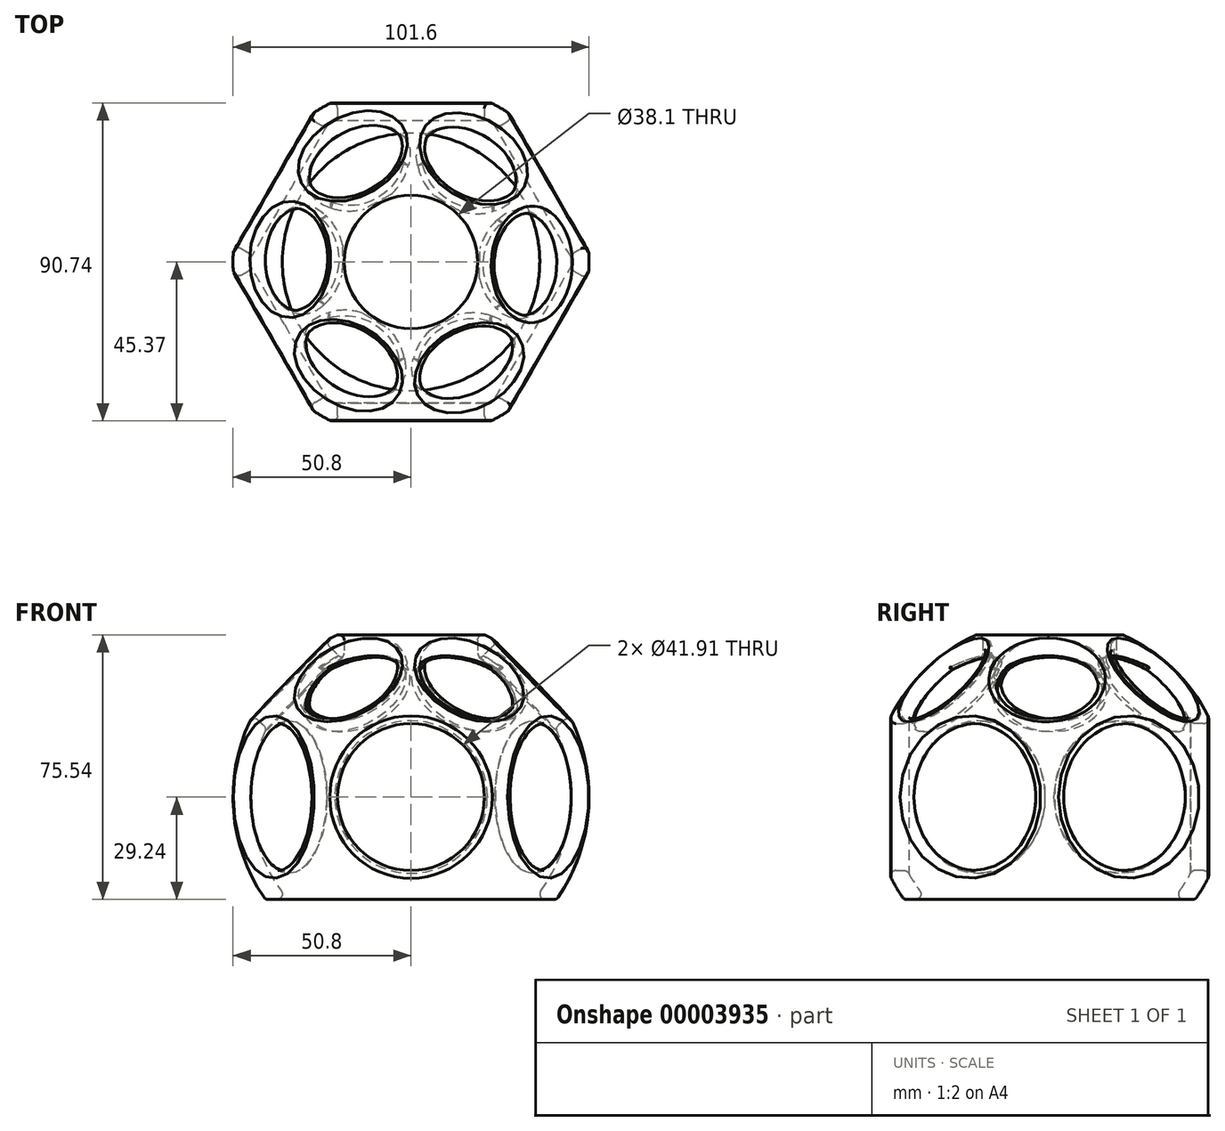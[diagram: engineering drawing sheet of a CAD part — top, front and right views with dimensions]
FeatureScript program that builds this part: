
annotation { "Feature Type Name" : "Feature", "Feature Type Description" : "" }
export const myFeature = defineFeature(function(context is Context, id is Id, definition is map)
    precondition{}
    {
        {
            var Q0;
            Q0=qCreatedBy(makeId("Front.planeOp"),FACE);
            var sketch = newSketch(context, id + "F0", { "sketchPlane" : qUnion([Q0])});
            skArc(sketch, "E0", {"start": v(0, 50.8) * mm, "mid": v(-42.5, 27.81) * mm, "end": v(-46.55, -20.35) * mm});
            skLineSegment(sketch, "E1", {"start": v(-40.94, -20.35) * mm, "end": v(0, 0) * mm, "construction": true});
            skLineSegment(sketch, "E2", {"start": v(0, 0) * mm, "end": v(0, 50.8) * mm, "construction": true});
            skArc(sketch, "E3", {"start": v(-27.63, 36.42) * mm, "mid": v(-44.51, 10.44) * mm, "end": v(-40.94, -20.35) * mm});
            skLineSegment(sketch, "E4", {"start": v(-40.94, -20.35) * mm, "end": v(-46.55, -20.35) * mm});
            skPoint(sketch, "E5.orphan", {"position": v(-45.5, -22.6) * mm});
            skArc(sketch, "E6", {"start": v(-46.55, -20.35) * mm, "mid": v(-44.27, -24.92) * mm, "end": v(-41.54, -29.24) * mm});
            skArc(sketch, "E7", {"start": v(-40.94, -20.35) * mm, "mid": v(-38.3, -24.96) * mm, "end": v(-35.15, -29.24) * mm});
            skLineSegment(sketch, "E8", {"start": v(-41.54, -29.24) * mm, "end": v(-35.15, -29.24) * mm});
            skLineSegment(sketch, "E9", {"start": v(0, 50.8) * mm, "end": v(0, 42.76) * mm});
            skArc(sketch, "E10", {"start": v(0, 42.76) * mm, "mid": v(-14.22, 41.33) * mm, "end": v(-27.63, 36.42) * mm});
            skSolve(sketch);
        }
        {
            var Q0;
            Q0=sQuery(id+"F0.wireOp",EDGE,"E1");
            cPlane(context, id + "F1", {"entities" : qUnion([Q0]), "cplaneType" : CPlaneType.LINE_ANGLE, "offset" : 152.4 * mm, "angle" : 51 * degree, "width" : 152.4 * mm, "height" : 152.4 * mm});
        }
        {
            var Q0;
            Q0=makeQuery(id+"F0.imprint","IMPRINT",FACE,{"disambiguationData":[TD([[makeQuery(id+"F0.imprint","IMPRINT",EDGE,{"derivedFrom":sQuery(id+"F0.wireOp",EDGE,"E0")}),1.0]])]});
            var Q1;
            Q1=makeQuery(id+"F0.imprint","IMPRINT",FACE,{"disambiguationData":[TD([[makeQuery(id+"F0.imprint","IMPRINT",EDGE,{"derivedFrom":sQuery(id+"F0.wireOp",EDGE,"E4")}),1.0]])]});
            var Q2;
            Q2=sQuery(id+"F0.wireOp",EDGE,"E2");
            revolve(context, id + "F2", {"entities" : qUnion([Q0, Q1]), "axis" : qUnion([Q2]), "revolveType" : RevolveType.FULL});
        }
        {
            var Q0;
            Q0=qCreatedBy(makeId("Top.planeOp"),FACE);
            var sketch = newSketch(context, id + "F3", { "sketchPlane" : qUnion([Q0])});
            skCircle(sketch, "E11", {"center": v(0, 0) * mm, "radius": 19.05 * mm});
            skSolve(sketch);
        }
        {
            var Q0;
            Q0=makeQuery(id+"F3.imprint","IMPRINT",FACE,{"disambiguationData":[TD([[makeQuery(id+"F3.imprint","IMPRINT",EDGE,{"derivedFrom":sQuery(id+"F3.wireOp",EDGE,"E11")}),1.0]])]});
            extrude(context, id + "F4", {"entities" : qUnion([Q0]), "operationType" : NewBodyOperationType.REMOVE, "endBound" : BoundingType.SYMMETRIC, "depth" : 101.6 * mm});
        }
        {
            var Q0;
            Q0=qCreatedBy(makeId("Front.planeOp"),FACE);
            var sketch = newSketch(context, id + "F5", { "sketchPlane" : qUnion([Q0])});
            skCircle(sketch, "E12", {"center": v(0, 0) * mm, "radius": 20.96 * mm});
            skSolve(sketch);
        }
        {
            var Q0;
            Q0=makeQuery(id+"F5.imprint","IMPRINT",FACE,{"disambiguationData":[TD([[makeQuery(id+"F5.imprint","IMPRINT",EDGE,{"derivedFrom":sQuery(id+"F5.wireOp",EDGE,"E12")}),1.0]])]});
            var Q1;
            Q1=sQuery(id+"F5.wireOp",EDGE,"E12");
            extrude(context, id + "F6", {"entities" : qUnion([Q0]), "surfaceEntities" : qUnion([Q1]), "depth" : 76.2 * mm});
        }
        {
            var Q0;
            Q0=makeQuery(id+"F6.opExtrude","SWEPT_FACE",FACE,{"disambiguationData":[OSD([sQuery(id+"F5.wireOp",EDGE,"E12")])]});
            var Q1;
            Q1=makeQuery(id+"F6.opExtrude","SWEPT_BODY",BODY,{"disambiguationData":[OSD([sQuery(id+"F5.wireOp",EDGE,"E12")])]});
            var Q2;
            Q2=makeQuery(id+"F4.boolean.opBoolean","COPY",FACE,{"derivedFrom":makeQuery(id+"F4.opExtrude","SWEPT_FACE",FACE,{"disambiguationData":[OSD([sQuery(id+"F3.wireOp",EDGE,"E11")])]})});
            circularPattern(context, id + "F7", {"entities" : qUnion([Q1]), "axis" : qUnion([Q2]), "angle" : 60 * degree, "instanceCount" : 6});
        }
        {
            var Q0;
            Q0=makeQuery(id+"F6.opExtrude","SWEPT_BODY",BODY,{"disambiguationData":[OSD([sQuery(id+"F5.wireOp",EDGE,"E12")])]});
            var Q1;
            Q1=makeQuery(id+"F7.opPattern","COPY",BODY,{"derivedFrom":makeQuery(id+"F6.opExtrude","SWEPT_BODY",BODY,{"disambiguationData":[OSD([sQuery(id+"F5.wireOp",EDGE,"E12")])]}),"instanceName":"5"});
            var Q2;
            Q2=makeQuery(id+"F7.opPattern","COPY",BODY,{"derivedFrom":makeQuery(id+"F6.opExtrude","SWEPT_BODY",BODY,{"disambiguationData":[OSD([sQuery(id+"F5.wireOp",EDGE,"E12")])]}),"instanceName":"4"});
            var Q3;
            Q3=makeQuery(id+"F7.opPattern","COPY",BODY,{"derivedFrom":makeQuery(id+"F6.opExtrude","SWEPT_BODY",BODY,{"disambiguationData":[OSD([sQuery(id+"F5.wireOp",EDGE,"E12")])]}),"instanceName":"3"});
            var Q4;
            Q4=makeQuery(id+"F7.opPattern","COPY",BODY,{"derivedFrom":makeQuery(id+"F6.opExtrude","SWEPT_BODY",BODY,{"disambiguationData":[OSD([sQuery(id+"F5.wireOp",EDGE,"E12")])]}),"instanceName":"2"});
            var Q5;
            Q5=makeQuery(id+"F7.opPattern","COPY",BODY,{"derivedFrom":makeQuery(id+"F6.opExtrude","SWEPT_BODY",BODY,{"disambiguationData":[OSD([sQuery(id+"F5.wireOp",EDGE,"E12")])]}),"instanceName":"1"});
            var Q6;
            Q6=makeQuery(id+"F2.opRevolve","SWEPT_BODY",BODY,{"disambiguationData":[OSD([sQuery(id+"F0.wireOp",EDGE,"E0"),sQuery(id+"F0.wireOp",EDGE,"E1"),sQuery(id+"F0.wireOp",EDGE,"E2")])]});
            booleanBodies(context, id + "F8", {"operationType" : BooleanOperationType.SUBTRACTION, "tools" : qUnion([Q0, Q1, Q2, Q3, Q4, Q5]), "targets" : qUnion([Q6])});
        }
        {
            var Q0;
            Q0=qCreatedBy(id+"F1.planeOp",FACE);
            var sketch = newSketch(context, id + "F9", { "sketchPlane" : qUnion([Q0])});
            skCircle(sketch, "E13", {"center": v(0, 0) * mm, "radius": 14.6 * mm});
            skLineSegment(sketch, "E14", {"start": v(0, 0) * mm, "end": v(14.6, 0) * mm, "construction": true});
            skSolve(sketch);
        }
        {
            var Q0;
            Q0 = qSketchRegion(id + "F9", true);
            extrude(context, id + "F10", {"entities" : qUnion([Q0]), "depth" : 76.2 * mm});
        }
        {
            var Q0;
            Q0=makeQuery(id+"F10.opExtrude","SWEPT_BODY",BODY,{"disambiguationData":[OSD([sQuery(id+"F9.wireOp",EDGE,"E13")])]});
            var Q1;
            Q1=makeQuery(id+"F4.boolean.opBoolean","INTERSECT",EDGE,{"derivedFrom":[makeQuery(id+"F2.opRevolve","SWEPT_FACE",FACE,{"disambiguationData":[OSD([sQuery(id+"F0.wireOp",EDGE,"E0")])]}),makeQuery(id+"F4.opExtrude","SWEPT_FACE",FACE,{"disambiguationData":[OSD([sQuery(id+"F3.wireOp",EDGE,"E11")])]})]});
            circularPattern(context, id + "F11", {"entities" : qUnion([Q0]), "axis" : qUnion([Q1]), "angle" : 60 * degree, "instanceCount" : 6});
        }
        {
            var Q0;
            Q0=makeQuery(id+"F11.opPattern","COPY",BODY,{"derivedFrom":makeQuery(id+"F10.opExtrude","SWEPT_BODY",BODY,{"disambiguationData":[OSD([sQuery(id+"F9.wireOp",EDGE,"E13")])]}),"instanceName":"3"});
            var Q1;
            Q1=makeQuery(id+"F11.opPattern","COPY",BODY,{"derivedFrom":makeQuery(id+"F10.opExtrude","SWEPT_BODY",BODY,{"disambiguationData":[OSD([sQuery(id+"F9.wireOp",EDGE,"E13")])]}),"instanceName":"2"});
            var Q2;
            Q2=makeQuery(id+"F11.opPattern","COPY",BODY,{"derivedFrom":makeQuery(id+"F10.opExtrude","SWEPT_BODY",BODY,{"disambiguationData":[OSD([sQuery(id+"F9.wireOp",EDGE,"E13")])]}),"instanceName":"1"});
            var Q3;
            Q3=makeQuery(id+"F10.opExtrude","SWEPT_BODY",BODY,{"disambiguationData":[OSD([sQuery(id+"F9.wireOp",EDGE,"E13")])]});
            var Q4;
            Q4=makeQuery(id+"F11.opPattern","COPY",BODY,{"derivedFrom":makeQuery(id+"F10.opExtrude","SWEPT_BODY",BODY,{"disambiguationData":[OSD([sQuery(id+"F9.wireOp",EDGE,"E13")])]}),"instanceName":"5"});
            var Q5;
            Q5=makeQuery(id+"F11.opPattern","COPY",BODY,{"derivedFrom":makeQuery(id+"F10.opExtrude","SWEPT_BODY",BODY,{"disambiguationData":[OSD([sQuery(id+"F9.wireOp",EDGE,"E13")])]}),"instanceName":"4"});
            var Q6;
            Q6=makeQuery(id+"F2.opRevolve","SWEPT_BODY",BODY,{"disambiguationData":[OSD([sQuery(id+"F0.wireOp",EDGE,"E0"),sQuery(id+"F0.wireOp",EDGE,"E1"),sQuery(id+"F0.wireOp",EDGE,"E2")])]});
            booleanBodies(context, id + "F12", {"operationType" : BooleanOperationType.SUBTRACTION, "tools" : qUnion([Q0, Q1, Q2, Q3, Q4, Q5]), "targets" : qUnion([Q6])});
        }
        {
            var Q0;
            Q0=makeQuery(id+"F2.opRevolve","SWEPT_FACE",FACE,{"disambiguationData":[OSD([sQuery(id+"F0.wireOp",EDGE,"E0"),sQuery(id+"F0.wireOp",EDGE,"E6")])]});
            var Q1;
            Q1=makeQuery(id+"F2.opRevolve","SWEPT_FACE",FACE,{"disambiguationData":[OSD([sQuery(id+"F0.wireOp",EDGE,"E3"),sQuery(id+"F0.wireOp",EDGE,"E7")])]});
            var Q2;
            Q2=makeQuery(id+"F2.opRevolve","SWEPT_FACE",FACE,{"disambiguationData":[OSD([sQuery(id+"F0.wireOp",EDGE,"E10")])]});
            fillet(context, id + "F13", {"entities" : qUnion([Q0, Q1, Q2]), "radius" : 1.52 * mm, "tangentPropagation" : true, "allowEdgeOverflow" : false});
        }
    });
